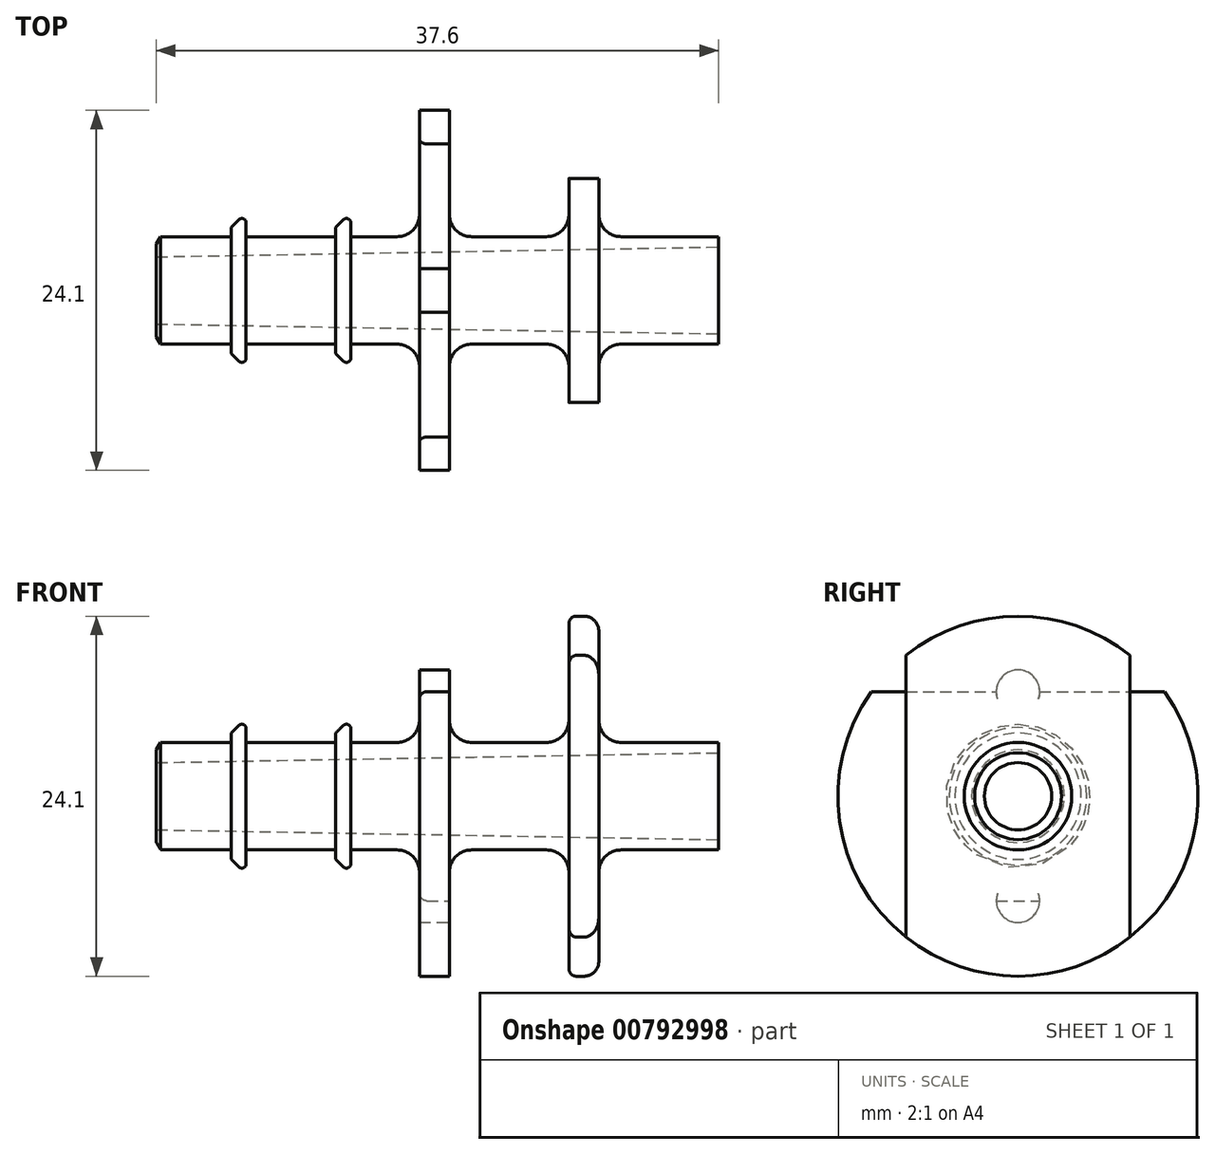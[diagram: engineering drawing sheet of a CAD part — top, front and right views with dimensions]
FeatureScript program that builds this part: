
annotation { "Feature Type Name" : "Feature", "Feature Type Description" : "" }
export const myFeature = defineFeature(function(context is Context, id is Id, definition is map)
    precondition{}
    {
        {
            var Q0;
            Q0=qCreatedBy(makeId("Front.planeOp"),FACE);
            var sketch = newSketch(context, id + "F0", { "sketchPlane" : qUnion([Q0])});
            skLineSegment(sketch, "E0", {"start": v(1, 3.6) * mm, "end": v(6, 3.6) * mm});
            skLineSegment(sketch, "E1", {"start": v(20.6, 3.6) * mm, "end": v(20.6, 12.05) * mm});
            skLineSegment(sketch, "E2", {"start": v(18.6, 12.05) * mm, "end": v(20.6, 12.05) * mm});
            skLineSegment(sketch, "E3", {"start": v(18.6, 12.05) * mm, "end": v(18.6, 3.6) * mm});
            skLineSegment(sketch, "E4", {"start": v(6, 3.6) * mm, "end": v(6, 4.23) * mm});
            skLineSegment(sketch, "E5", {"start": v(7, 4.6) * mm, "end": v(7, 3.6) * mm});
            skLineSegment(sketch, "E6", {"start": v(13, 3.6) * mm, "end": v(13, 4.23) * mm});
            skLineSegment(sketch, "E7", {"start": v(14, 4.6) * mm, "end": v(14, 3.6) * mm});
            skLineSegment(sketch, "E8", {"start": v(28.6, 3.6) * mm, "end": v(28.6, 12.05) * mm});
            skLineSegment(sketch, "E9", {"start": v(28.6, 12.05) * mm, "end": v(30.6, 12.05) * mm});
            skLineSegment(sketch, "E10", {"start": v(30.6, 12.05) * mm, "end": v(30.6, 3.6) * mm});
            skLineSegment(sketch, "E11", {"start": v(6.5, 4.73) * mm, "end": v(6, 4.23) * mm});
            skPoint(sketch, "E12.orphan", {"position": v(6, 4.86) * mm});
            skLineSegment(sketch, "E13", {"start": v(13, 4.23) * mm, "end": v(13.5, 4.73) * mm});
            skPoint(sketch, "E14.orphan", {"position": v(13, 4.86) * mm});
            skLineSegment(sketch, "E15", {"start": v(1, 3.6) * mm, "end": v(1, 2.25) * mm});
            skLineSegment(sketch, "E16.trimOffspring", {"start": v(7, 3.6) * mm, "end": v(13, 3.6) * mm});
            skLineSegment(sketch, "E17.trimOffspring", {"start": v(14, 3.6) * mm, "end": v(18.6, 3.6) * mm});
            skLineSegment(sketch, "E18", {"start": v(38.6, 3.6) * mm, "end": v(38.6, 2.9) * mm});
            skLineSegment(sketch, "E19", {"start": v(1, 2.25) * mm, "end": v(38.6, 2.9) * mm});
            skPoint(sketch, "E20.orphan", {"position": v(1, -6.05) * mm});
            skPoint(sketch, "E21.orphan", {"position": v(38.6, -6.05) * mm});
            skLineSegment(sketch, "E22", {"start": v(0, 0) * mm, "end": v(42.86, 0) * mm, "construction": true});
            skLineSegment(sketch, "E23.trimOffspring", {"start": v(20.6, 3.6) * mm, "end": v(28.6, 3.6) * mm});
            skLineSegment(sketch, "E24.trimOffspring", {"start": v(30.6, 3.6) * mm, "end": v(38.6, 3.6) * mm});
            skArc(sketch, "E25", {"start": v(7, 4.6) * mm, "mid": v(6.79, 4.8) * mm, "end": v(6.5, 4.73) * mm});
            skArc(sketch, "E26", {"start": v(14, 4.6) * mm, "mid": v(13.79, 4.8) * mm, "end": v(13.5, 4.73) * mm});
            skSolve(sketch);
        }
        {
            var Q0;
            Q0=makeQuery(id+"F0.imprint","IMPRINT",FACE,{"disambiguationData":[TD([[makeQuery(id+"F0.imprint","IMPRINT",EDGE,{"derivedFrom":sQuery(id+"F0.wireOp",EDGE,"E0")}),-1.0]])]});
            var Q1;
            {var subQ0=sQuery(id+"F0.wireOp",EDGE,"E1");Q1=makeQuery(id+"F0.imprint","IMPRINT",FACE,{"disambiguationData":[TD([[makeQuery(id+"F0.imprint","IMPRINT",EDGE,{"derivedFrom":subQ0}),1.0]])]});}
            var Q2;
            {var subQ0=sQuery(id+"F0.wireOp",EDGE,"E8");Q2=makeQuery(id+"F0.imprint","IMPRINT",FACE,{"disambiguationData":[TD([[makeQuery(id+"F0.imprint","IMPRINT",EDGE,{"derivedFrom":subQ0}),-1.0]])]});}
            var Q3;
            Q3=sQuery(id+"F0.wireOp",EDGE,"E22");
            revolve(context, id + "F1", {"surfaceOperationType" : NewSurfaceOperationType.NEW, "entities" : qUnion([Q0, Q1, Q2]), "axis" : qUnion([Q3]), "revolveType" : RevolveType.FULL});
        }
        {
            var Q0;
            Q0=makeQuery(id+"F1.opRevolve","SWEPT_EDGE",EDGE,{"disambiguationData":[OSD([sQuery(id+"F0.wireOp",EDGE,"E3"),sQuery(id+"F0.wireOp",EDGE,"E17.trimOffspring")])]});
            var Q1;
            Q1=makeQuery(id+"F1.opRevolve","SWEPT_EDGE",EDGE,{"disambiguationData":[OSD([sQuery(id+"F0.wireOp",EDGE,"E1"),sQuery(id+"F0.wireOp",EDGE,"E23.trimOffspring")])]});
            var Q2;
            Q2=makeQuery(id+"F1.opRevolve","SWEPT_EDGE",EDGE,{"disambiguationData":[OSD([sQuery(id+"F0.wireOp",EDGE,"E8"),sQuery(id+"F0.wireOp",EDGE,"E23.trimOffspring")])]});
            var Q3;
            Q3=makeQuery(id+"F1.opRevolve","SWEPT_EDGE",EDGE,{"disambiguationData":[OSD([sQuery(id+"F0.wireOp",EDGE,"E10"),sQuery(id+"F0.wireOp",EDGE,"E24.trimOffspring")])]});
            fillet(context, id + "F2", {"entities" : qUnion([Q0, Q1, Q2, Q3]), "radius" : 1.5 * mm, "tangentPropagation" : true, "allowEdgeOverflow" : false});
        }
        {
            var Q0;
            Q0=makeQuery(id+"F1.opRevolve","SWEPT_EDGE",EDGE,{"disambiguationData":[OSD([sQuery(id+"F0.wireOp",EDGE,"E0"),sQuery(id+"F0.wireOp",EDGE,"E15")])]});
            chamfer(context, id + "F3", {"entities" : qUnion([Q0]), "chamferType" : ChamferType.OFFSET_ANGLE, "width" : .5 * mm, "oppositeDirection" : false, "angle" : 30 * degree, "tangentPropagation" : true});
        }
        {
            var Q0;
            Q0=makeQuery(id+"F1.opRevolve","SWEPT_FACE",FACE,{"disambiguationData":[OSD([sQuery(id+"F0.wireOp",EDGE,"E10")])]});
            var sketch = newSketch(context, id + "F4", { "sketchPlane" : qUnion([Q0])});
            skLineSegment(sketch, "E27", {"start": v(7.5, 14.83) * mm, "end": v(7.5, -15.37) * mm});
            skLineSegment(sketch, "E28", {"start": v(0, 1.29) * mm, "end": v(0, -1.74) * mm, "construction": true});
            skLineSegment(sketch, "E29.MirrorCS", {"start": v(-7.5, 14.83) * mm, "end": v(-7.5, -15.37) * mm});
            skSolve(sketch);
        }
        {
            var Q0;
            {var subQ0=sQuery(id+"F4.wireOp",EDGE,"E29.MirrorCS");var subQ1=makeQuery(id+"F1.opRevolve","SWEPT_EDGE",EDGE,{"disambiguationData":[OSD([sQuery(id+"F0.wireOp",EDGE,"E9"),sQuery(id+"F0.wireOp",EDGE,"E10")])]});var subQ2=makeQuery(id+"F4.imprint","INTERSECT",VERTEX,{"disambiguationData":[OD(0.0)],"derivedFrom":[subQ1,subQ0]});Q0=makeQuery(id+"F4.imprint","IMPRINT",FACE,{"disambiguationData":[TD([[makeQuery(id+"F4.imprint","IMPRINT",EDGE,{"disambiguationData":[TD([[subQ2,1.0]])],"derivedFrom":subQ0}),-1.0]])]});}
            var Q1;
            {var subQ0=sQuery(id+"F4.wireOp",EDGE,"E27");var subQ1=makeQuery(id+"F1.opRevolve","SWEPT_EDGE",EDGE,{"disambiguationData":[OSD([sQuery(id+"F0.wireOp",EDGE,"E9"),sQuery(id+"F0.wireOp",EDGE,"E10")])]});var subQ2=makeQuery(id+"F4.imprint","INTERSECT",VERTEX,{"disambiguationData":[OD(0.0)],"derivedFrom":[subQ1,subQ0]});Q1=makeQuery(id+"F4.imprint","IMPRINT",FACE,{"disambiguationData":[TD([[makeQuery(id+"F4.imprint","IMPRINT",EDGE,{"disambiguationData":[TD([[subQ2,1.0]])],"derivedFrom":subQ0}),1.0]])]});}
            extrude(context, id + "F5", {"entities" : qUnion([Q0, Q1]), "operationType" : NewBodyOperationType.REMOVE, "oppositeDirection" : true, "depth" : 3.9 * mm, "offsetDistance" : 25 * mm});
        }
        {
            var Q0;
            Q0=makeQuery(id+"F1.opRevolve","SWEPT_FACE",FACE,{"disambiguationData":[OSD([sQuery(id+"F0.wireOp",EDGE,"E1")])]});
            var sketch = newSketch(context, id + "F6", { "sketchPlane" : qUnion([Q0])});
            skLineSegment(sketch, "E30", {"start": v(-14.15, 7) * mm, "end": v(15.53, 7) * mm});
            skArc(sketch, "E31", {"start": v(1.45, 7) * mm, "mid": v(0, 8.45) * mm, "end": v(-1.45, 7) * mm});
            skLineSegment(sketch, "E32", {"start": v(-1.73, 0) * mm, "end": v(1.76, 0) * mm, "construction": true});
            skLineSegment(sketch, "E33.MirrorCS", {"start": v(-14.15, -7) * mm, "end": v(15.53, -7) * mm});
            skArc(sketch, "E34.MirrorCS", {"start": v(1.45, -7) * mm, "mid": v(0, -8.45) * mm, "end": v(-1.45, -7) * mm});
            skLineSegment(sketch, "E35", {"start": v(-14.15, 7) * mm, "end": v(-0.85, 15.14) * mm});
            skLineSegment(sketch, "E36", {"start": v(-0.85, 15.14) * mm, "end": v(15.53, 7) * mm});
            skLineSegment(sketch, "E37", {"start": v(-14.15, -7) * mm, "end": v(0.87, -15.68) * mm});
            skLineSegment(sketch, "E38", {"start": v(0.87, -15.68) * mm, "end": v(15.53, -7) * mm});
            skSolve(sketch);
        }
        {
            var Q0;
            {var subQ0=sQuery(id+"F6.wireOp",EDGE,"E31");Q0=makeQuery(id+"F6.imprint","IMPRINT",FACE,{"disambiguationData":[TD([[makeQuery(id+"F6.imprint","IMPRINT",EDGE,{"derivedFrom":subQ0}),-1.0]])]});}
            var Q1;
            {var subQ0=sQuery(id+"F6.wireOp",EDGE,"E34.MirrorCS");Q1=makeQuery(id+"F6.imprint","IMPRINT",FACE,{"disambiguationData":[TD([[makeQuery(id+"F6.imprint","IMPRINT",EDGE,{"derivedFrom":subQ0}),1.0]])]});}
            extrude(context, id + "F7", {"entities" : qUnion([Q0, Q1]), "operationType" : NewBodyOperationType.REMOVE, "oppositeDirection" : true, "depth" : 5 * mm, "offsetDistance" : 25 * mm});
        }
        {
            var Q0;
            Q0=makeQuery(id+"F5.boolean.opBoolean","SPLIT",EDGE,{"disambiguationData":[OD(0.0)],"derivedFrom":makeQuery(id+"F1.opRevolve","SWEPT_EDGE",EDGE,{"disambiguationData":[OSD([sQuery(id+"F0.wireOp",EDGE,"E8"),sQuery(id+"F0.wireOp",EDGE,"E9")])]})});
            var Q1;
            Q1=makeQuery(id+"F5.boolean.opBoolean","SPLIT",EDGE,{"disambiguationData":[OD(1.0)],"derivedFrom":makeQuery(id+"F1.opRevolve","SWEPT_EDGE",EDGE,{"disambiguationData":[OSD([sQuery(id+"F0.wireOp",EDGE,"E8"),sQuery(id+"F0.wireOp",EDGE,"E9")])]})});
            fillet(context, id + "F8", {"entities" : qUnion([Q0, Q1]), "radius" : .5 * mm, "tangentPropagation" : true, "allowEdgeOverflow" : false});
        }
        {
            var Q0;
            Q0=makeQuery(id+"F5.boolean.opBoolean","SPLIT",EDGE,{"disambiguationData":[OD(0.0)],"derivedFrom":makeQuery(id+"F1.opRevolve","SWEPT_EDGE",EDGE,{"disambiguationData":[OSD([sQuery(id+"F0.wireOp",EDGE,"E9"),sQuery(id+"F0.wireOp",EDGE,"E10")])]})});
            var Q1;
            Q1=makeQuery(id+"F5.boolean.opBoolean","SPLIT",EDGE,{"disambiguationData":[OD(1.0)],"derivedFrom":makeQuery(id+"F1.opRevolve","SWEPT_EDGE",EDGE,{"disambiguationData":[OSD([sQuery(id+"F0.wireOp",EDGE,"E9"),sQuery(id+"F0.wireOp",EDGE,"E10")])]})});
            fillet(context, id + "F9", {"entities" : qUnion([Q0, Q1]), "radius" : 1 * mm, "tangentPropagation" : true, "allowEdgeOverflow" : false});
        }
        {
            var Q0;
            {var subQ0=sQuery(id+"F6.wireOp",EDGE,"E30");Q0=makeQuery(id+"F7.boolean.opBoolean","INTERSECT",EDGE,{"derivedFrom":[makeQuery(id+"F1.opRevolve","SWEPT_FACE",FACE,{"disambiguationData":[OSD([sQuery(id+"F0.wireOp",EDGE,"E3")])]}),makeQuery(id+"F7.opExtrude","SWEPT_FACE",FACE,{"disambiguationData":[OSD([subQ0]),TDD([makeQuery(id+"F6.imprint","IMPRINT",EDGE,{"disambiguationData":[TD([[makeQuery(id+"F6.imprint","INTERSECT",VERTEX,{"disambiguationData":[OD(1.0)],"derivedFrom":[subQ0,sQuery(id+"F6.wireOp",EDGE,"E31")]}),1.0]])],"derivedFrom":subQ0})])]})]});}
            var Q1;
            {var subQ0=sQuery(id+"F6.wireOp",EDGE,"E30");Q1=makeQuery(id+"F7.boolean.opBoolean","COPY",EDGE,{"derivedFrom":makeQuery(id+"F7.opExtrude","CAP_EDGE",EDGE,{"disambiguationData":[OSD([subQ0]),TDD([makeQuery(id+"F6.imprint","IMPRINT",EDGE,{"disambiguationData":[TD([[makeQuery(id+"F6.imprint","INTERSECT",VERTEX,{"disambiguationData":[OD(1.0)],"derivedFrom":[subQ0,sQuery(id+"F6.wireOp",EDGE,"E31")]}),1.0]])],"derivedFrom":subQ0})])],"isStart":true})});}
            var Q2;
            {var subQ0=sQuery(id+"F6.wireOp",EDGE,"E30");Q2=makeQuery(id+"F7.boolean.opBoolean","COPY",EDGE,{"derivedFrom":makeQuery(id+"F7.opExtrude","CAP_EDGE",EDGE,{"disambiguationData":[OSD([subQ0]),TDD([makeQuery(id+"F6.imprint","IMPRINT",EDGE,{"disambiguationData":[TD([[makeQuery(id+"F6.imprint","INTERSECT",VERTEX,{"disambiguationData":[OD(0.0)],"derivedFrom":[subQ0,sQuery(id+"F6.wireOp",EDGE,"E31")]}),-1.0]])],"derivedFrom":subQ0})])],"isStart":true})});}
            var Q3;
            {var subQ0=sQuery(id+"F6.wireOp",EDGE,"E30");Q3=makeQuery(id+"F7.boolean.opBoolean","INTERSECT",EDGE,{"derivedFrom":[makeQuery(id+"F1.opRevolve","SWEPT_FACE",FACE,{"disambiguationData":[OSD([sQuery(id+"F0.wireOp",EDGE,"E3")])]}),makeQuery(id+"F7.opExtrude","SWEPT_FACE",FACE,{"disambiguationData":[OSD([subQ0]),TDD([makeQuery(id+"F6.imprint","IMPRINT",EDGE,{"disambiguationData":[TD([[makeQuery(id+"F6.imprint","INTERSECT",VERTEX,{"disambiguationData":[OD(0.0)],"derivedFrom":[subQ0,sQuery(id+"F6.wireOp",EDGE,"E31")]}),-1.0]])],"derivedFrom":subQ0})])]})]});}
            var Q4;
            {var subQ0=sQuery(id+"F6.wireOp",EDGE,"E33.MirrorCS");Q4=makeQuery(id+"F7.boolean.opBoolean","INTERSECT",EDGE,{"derivedFrom":[makeQuery(id+"F1.opRevolve","SWEPT_FACE",FACE,{"disambiguationData":[OSD([sQuery(id+"F0.wireOp",EDGE,"E3")])]}),makeQuery(id+"F7.opExtrude","SWEPT_FACE",FACE,{"disambiguationData":[OSD([subQ0]),TDD([makeQuery(id+"F6.imprint","IMPRINT",EDGE,{"disambiguationData":[TD([[makeQuery(id+"F6.imprint","INTERSECT",VERTEX,{"disambiguationData":[OD(1.0)],"derivedFrom":[subQ0,sQuery(id+"F6.wireOp",EDGE,"E34.MirrorCS")]}),1.0]])],"derivedFrom":subQ0})])]})]});}
            var Q5;
            {var subQ0=sQuery(id+"F6.wireOp",EDGE,"E33.MirrorCS");Q5=makeQuery(id+"F7.boolean.opBoolean","COPY",EDGE,{"derivedFrom":makeQuery(id+"F7.opExtrude","CAP_EDGE",EDGE,{"disambiguationData":[OSD([subQ0]),TDD([makeQuery(id+"F6.imprint","IMPRINT",EDGE,{"disambiguationData":[TD([[makeQuery(id+"F6.imprint","INTERSECT",VERTEX,{"disambiguationData":[OD(1.0)],"derivedFrom":[subQ0,sQuery(id+"F6.wireOp",EDGE,"E34.MirrorCS")]}),1.0]])],"derivedFrom":subQ0})])],"isStart":true})});}
            var Q6;
            {var subQ0=sQuery(id+"F6.wireOp",EDGE,"E33.MirrorCS");Q6=makeQuery(id+"F7.boolean.opBoolean","INTERSECT",EDGE,{"derivedFrom":[makeQuery(id+"F1.opRevolve","SWEPT_FACE",FACE,{"disambiguationData":[OSD([sQuery(id+"F0.wireOp",EDGE,"E3")])]}),makeQuery(id+"F7.opExtrude","SWEPT_FACE",FACE,{"disambiguationData":[OSD([subQ0]),TDD([makeQuery(id+"F6.imprint","IMPRINT",EDGE,{"disambiguationData":[TD([[makeQuery(id+"F6.imprint","INTERSECT",VERTEX,{"disambiguationData":[OD(0.0)],"derivedFrom":[subQ0,sQuery(id+"F6.wireOp",EDGE,"E34.MirrorCS")]}),-1.0]])],"derivedFrom":subQ0})])]})]});}
            var Q7;
            {var subQ0=sQuery(id+"F6.wireOp",EDGE,"E33.MirrorCS");Q7=makeQuery(id+"F7.boolean.opBoolean","COPY",EDGE,{"derivedFrom":makeQuery(id+"F7.opExtrude","CAP_EDGE",EDGE,{"disambiguationData":[OSD([subQ0]),TDD([makeQuery(id+"F6.imprint","IMPRINT",EDGE,{"disambiguationData":[TD([[makeQuery(id+"F6.imprint","INTERSECT",VERTEX,{"disambiguationData":[OD(0.0)],"derivedFrom":[subQ0,sQuery(id+"F6.wireOp",EDGE,"E34.MirrorCS")]}),-1.0]])],"derivedFrom":subQ0})])],"isStart":true})});}
            fillet(context, id + "F10", {"entities" : qUnion([Q0, Q1, Q2, Q3, Q4, Q5, Q6, Q7]), "radius" : 0.5 * mm, "tangentPropagation" : true, "allowEdgeOverflow" : false});
        }
    });
